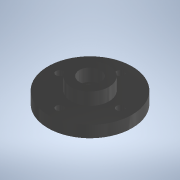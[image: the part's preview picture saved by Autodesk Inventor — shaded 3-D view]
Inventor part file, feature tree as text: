
AUTODESK INVENTOR PART (.ipt)
format: ipt  version: 2021 (Build 250183000, 183)  size: 127,488 bytes
history: native  units: mm
features: sketch x5, extrude x4
ambient origin geometry x8: Origin, YZ Plane, XZ Plane, XY Plane, X Axis, Y Axis, Z Axis, Center Point
bodies: Solid1 (feature_tree)
feature tree (9):
  extrude  "Extrusion1"  Depth=2.77mm TaperAngle=0.0deg
  extrude  "Extrusion2"  Depth=9.0mm
  extrude  "Extrusion3"  Depth=3.0mm TaperAngle=360.0deg
  extrude  "Extrusion4"  Depth=3.0mm
  sketch  "Sketch5"  dims[d16=5.0mm d17=0.0mm d18=4.0mm]
  sketch  "Sketch1"  dims[d0=20.0mm d1=2.77mm d2=0.0mm]
  sketch  "Sketch2"  dims[d3=5.0mm d4=9.0mm]
  sketch  "Sketch3"  dims[d5=3.0mm d6=0.0mm d9=40.0mm d11=360.0deg]
  sketch  "Sketch4"  dims[d13=3.0mm d14=0.0mm d15=5.0mm]
